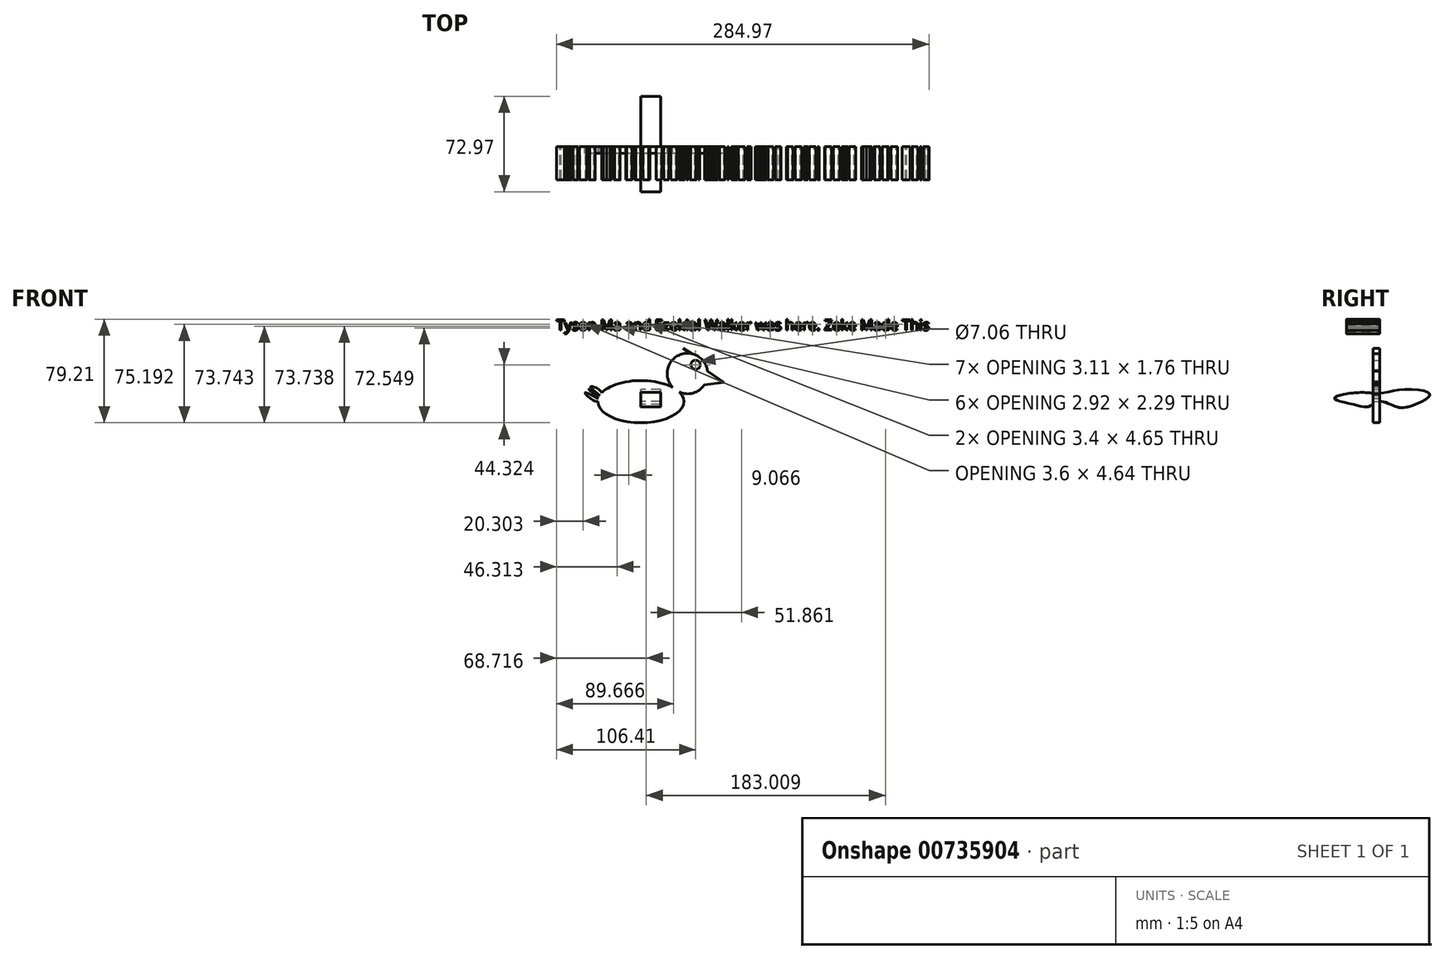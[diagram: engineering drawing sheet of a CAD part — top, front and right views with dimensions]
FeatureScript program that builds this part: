
annotation { "Feature Type Name" : "Feature", "Feature Type Description" : "" }
export const myFeature = defineFeature(function(context is Context, id is Id, definition is map)
    precondition{}
    {
        {
            var Q0;
            Q0=qCreatedBy(makeId("Front.planeOp"),FACE);
            var sketch = newSketch(context, id + "F0", { "sketchPlane" : qUnion([Q0])});
            skCircle(sketch, "E0", {"center": v(35.68, 12) * mm, "radius": 15.51 * mm});
            skEllipse(sketch, "E1", {"center": v(0, -9.47) * mm, "majorRadius": 32.9 * mm, "minorRadius": 16.15 * mm, "majorAxis": v(-1, 0)});
            skLineSegment(sketch, "E2", {"start": v(51.08, 13.8) * mm, "end": v(63.45, 5.33) * mm});
            skLineSegment(sketch, "E3", {"start": v(63.45, 5.33) * mm, "end": v(48.47, 3.24) * mm});
            skFitSpline(sketch, "E4", {"points": [v(-29.8, -2.63) * mm, v(-38.45, 1.85) * mm, v(-31.46, -4.73) * mm, v(-39.83, 0) * mm, v(-32.5, -6.91) * mm, v(-42.6, -2.54) * mm, v(-32.9, -9.47) * mm, v(-29.8, -2.63) * mm]});
            skCircle(sketch, "E5", {"center": v(41.91, 18.7) * mm, "radius": 3.53 * mm});
            skLineSegment(sketch, "E6", {"start": v(50.72, 8.24) * mm, "end": v(62.53, 5.2) * mm});
            skLineSegment(sketch, "E7", {"start": v(50.72, 8.24) * mm, "end": v(62.48, 5.99) * mm});
            skLineSegment(sketch, "E8", {"start": v(32.34, 31.4) * mm, "end": v(47.38, 18.7) * mm});
            skLineSegment(sketch, "E9", {"start": v(32.34, 31.4) * mm, "end": v(48.14, 21.24) * mm});
            skLineSegment(sketch, "E10", {"start": v(48.14, 21.24) * mm, "end": v(47.38, 18.7) * mm});
            skSolve(sketch);
        }
        {
            var Q0;
            Q0=qCreatedBy(makeId("Right.planeOp"),FACE);
            var sketch = newSketch(context, id + "F1", { "sketchPlane" : qUnion([Q0])});
            skFitSpline(sketch, "E11", {"points": [v(0, -3) * mm, v(21.13, 0) * mm, v(38.45, -4.16) * mm, v(25.05, -12.47) * mm, v(12.82, -13.4) * mm, v(0, -9.24) * mm, v(-7.97, -13.16) * mm, v(-18.36, -12) * mm, v(-34.52, -6.93) * mm, v(-16.51, -2.54) * mm, v(0, -3) * mm]});
            skSolve(sketch);
        }
        {
            var Q0;
            Q0=sQuery(id+"F1.wireOp",EDGE,"E11");
            extrude(context, id + "F2", {"bodyType" : ToolBodyType.SURFACE, "surfaceEntities" : qUnion([Q0]), "depth" : 15.24 * mm, "offsetDistance" : 25.4 * mm});
        }
        {
            var Q0;
            Q0=makeQuery(id+"F1.imprint","IMPRINT",FACE,{"disambiguationData":[TD([[makeQuery(id+"F1.imprint","IMPRINT",EDGE,{"derivedFrom":sQuery(id+"F1.wireOp",EDGE,"E11")}),-1.0]])]});
            extrude(context, id + "F3", {"entities" : qUnion([Q0]), "depth" : 15.24 * mm, "offsetDistance" : 25.4 * mm});
        }
        {
            var Q0;
            Q0 = qSketchRegion(id + "F0", true);
            extrude(context, id + "F4", {"entities" : qUnion([Q0]), "operationType" : NewBodyOperationType.ADD, "depth" : 5.08 * mm, "offsetDistance" : 25.4 * mm});
        }
        {
            var Q0;
            Q0=qCreatedBy(makeId("Front.planeOp"),FACE);
            var sketch = newSketch(context, id + "F5", { "sketchPlane" : qUnion([Q0])});
            skText(sketch, "E12", { "text": "Tyson Ma and Ezekial Walker was here. Zeke Made This", "fontName": "OpenSans-Regular.ttf"});
            const initialGuessF5  = {"E12": [-0.0646, 0.04515, 1, 0, 0.008]};
            skSetInitialGuess(sketch, initialGuessF5);
            skSolve(sketch);
        }
        {
            var Q0;
            Q0 = qSketchRegion(id + "F5", true);
            extrude(context, id + "F6", {"entities" : qUnion([Q0]), "depth" : 25.4 * mm, "offsetDistance" : 25.4 * mm});
        }
    });
